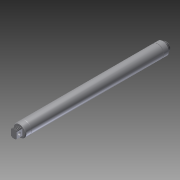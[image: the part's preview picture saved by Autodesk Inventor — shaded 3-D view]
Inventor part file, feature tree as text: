
AUTODESK INVENTOR PART (.ipt)
format: ipt  version: 2012 (Build 160160000, 160)  size: 152,576 bytes
history: native  units: in
note: dims shown in document units (in); Inventor stores cm internally (conversion verified against a paired STEP export)
features: extrude x7, sketch x3, thread x3, fillet x2, chamfer x2
ambient origin geometry x8: Origin, YZ Plane, XZ Plane, XY Plane, X Axis, Y Axis, Z Axis, Center Point
bodies: Solid1 (feature_tree)
feature tree (17):
  sketch  "Sketch1"  dims[d2=1.0in d3=1.125in d4=0.5in]
  extrude  "Extrusion1"  Depth=1.125in
  fillet  "Fillet1"  Radius=0.5in
  extrude  "Extrusion2"  Depth=0.559in
  extrude  "Extrusion3"  Depth=0.375in
  chamfer  "Chamfer1"  Distance=12.0in
  thread  "Thread1"  [1 undecoded]
  thread  "Thread2"  [1 undecoded]
  sketch  "Sketch2"  dims[d5=0.25in d6=0.559in]
  extrude  "Extrusion4"  Depth=1.0in TaperAngle=0.0deg
  extrude  "Extrusion5"  Depth=0.0625in TaperAngle=45.0deg
  fillet  "Fillet2"  Radius=1.0in
  extrude  "Extrusion6"  Depth=1.0in TaperAngle=0.0deg
  chamfer  "Chamfer2"  Distance=0.75in
  thread  "Thread3"  [1 undecoded]
  extrude  "Extrusion7"  Depth=0.25in
  sketch  "Sketch3"  dims[d7=0.2795in d8=0.375in d10=12.0in d11=0.0in d12=0.0312in d13=0.5in d14=0.0in d15=1.0in d16=0.0in d17=0.0625in d18=0.125in d19=45.0deg d20=1.0in d21=0.0in d22=1.0in d23=0.0in d24=0.75in d25=0.3125in d26=0.25in d27=0.5in d28=0.0in d29=0.75in d30=0.0in d31=0.0075in d32=0.75in d33=0.0in d34=0.0625in d35=0.125in d36=45.0deg d37=1.0in d38=0.0in d39=0.25in d40=0.2795in d41=0.559in d42=0.25in d43=1.0in d44=0.0in]
note: 3 required parameter values undecoded (feature->parameter linkage not recoverable at this tier; creation-order binding heuristic only, values carry confidence <= 0.55)
